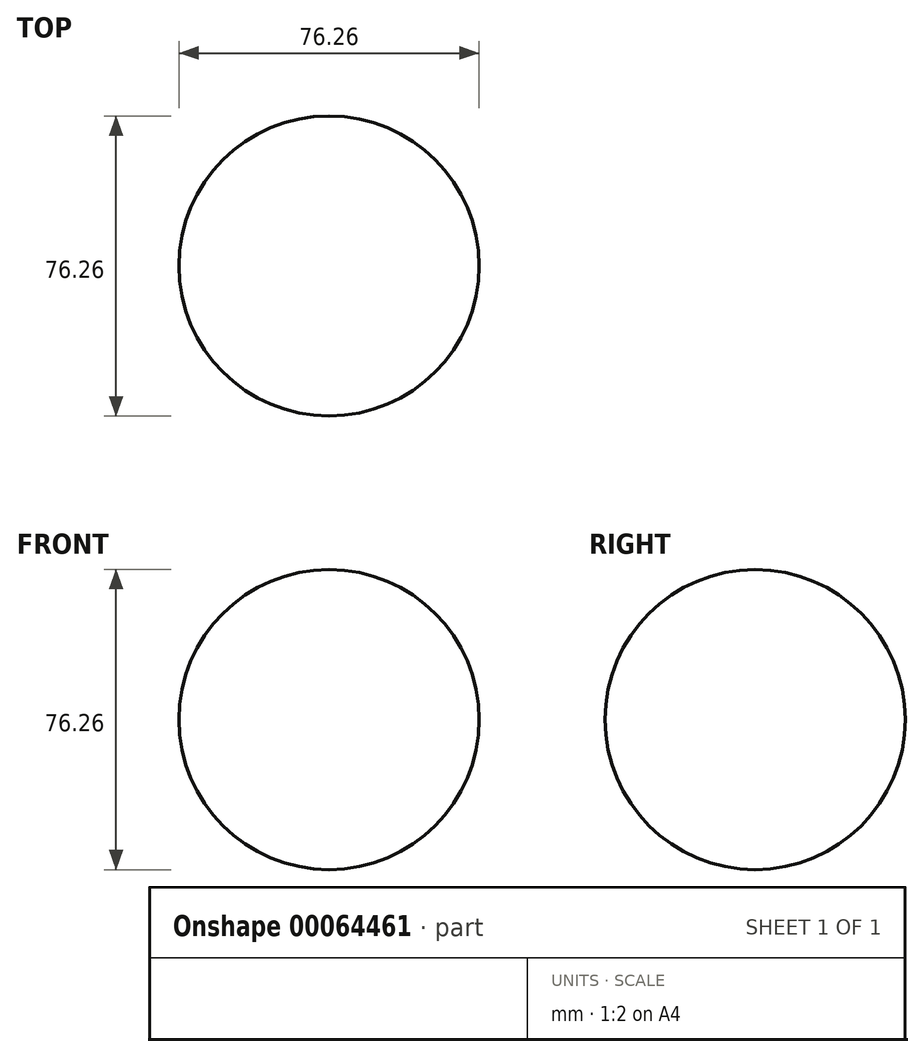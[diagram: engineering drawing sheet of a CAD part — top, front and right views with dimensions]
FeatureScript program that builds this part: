
annotation { "Feature Type Name" : "Feature", "Feature Type Description" : "" }
export const myFeature = defineFeature(function(context is Context, id is Id, definition is map)
    precondition{}
    {
        {
            var Q0;
            Q0=qCreatedBy(makeId("Front.planeOp"),FACE);
            var sketch = newSketch(context, id + "F0", { "sketchPlane" : qUnion([Q0])});
            skArc(sketch, "E0", {"start": v(0, -38.13) * mm, "mid": v(38.13, 0) * mm, "end": v(0, 38.13) * mm});
            skLineSegment(sketch, "E1", {"start": v(0, -38.13) * mm, "end": v(0, 38.13) * mm});
            skSolve(sketch);
        }
        {
            var Q0;
            Q0=makeQuery(id+"F0.imprint","IMPRINT",FACE,{"disambiguationData":[TD([[makeQuery(id+"F0.imprint","IMPRINT",EDGE,{"derivedFrom":sQuery(id+"F0.wireOp",EDGE,"E0")}),1.0]])]});
            var Q1;
            Q1=sQuery(id+"F0.wireOp",EDGE,"E1");
            revolve(context, id + "F1", {"entities" : qUnion([Q0]), "axis" : qUnion([Q1]), "revolveType" : RevolveType.FULL});
        }
    });
